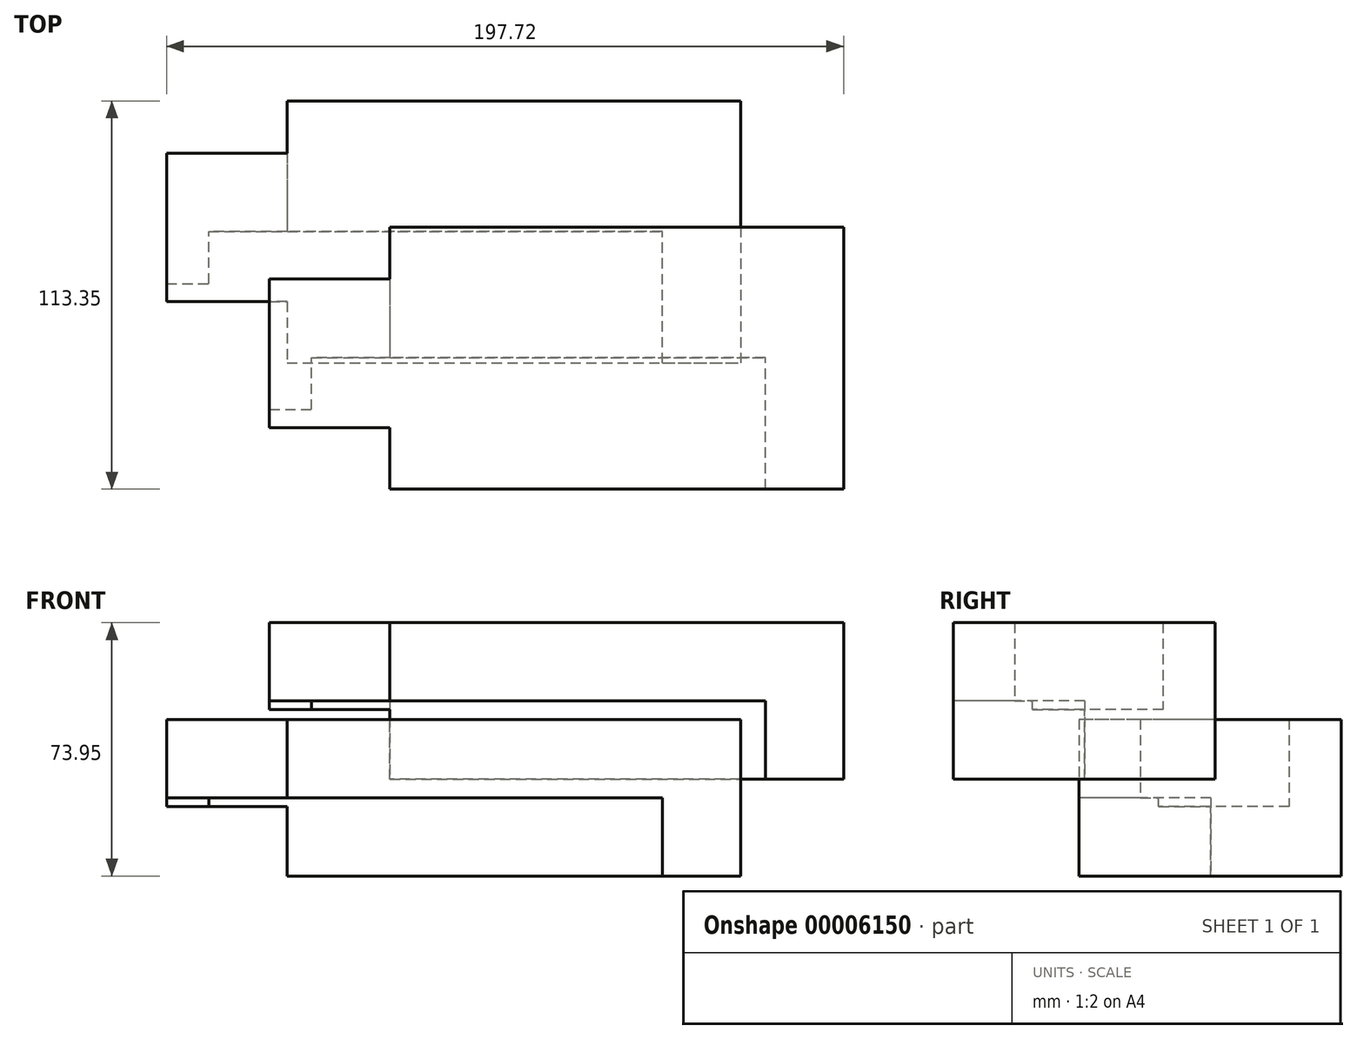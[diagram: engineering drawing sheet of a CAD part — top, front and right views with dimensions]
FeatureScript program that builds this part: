
annotation { "Feature Type Name" : "Feature", "Feature Type Description" : "" }
export const myFeature = defineFeature(function(context is Context, id is Id, definition is map)
    precondition{}
    {
        {
            var Q0;
            Q0=qCreatedBy(makeId("Top.planeOp"),FACE);
            var sketch = newSketch(context, id + "F0", { "sketchPlane" : qUnion([Q0])});
            skLineSegment(sketch, "E0.bottom", {"start": v(-122.75, 38.02) * mm, "end": v(9.77, 38.02) * mm});
            skLineSegment(sketch, "E0.top", {"start": v(-122.75, -38.52) * mm, "end": v(9.77, -38.52) * mm});
            skLineSegment(sketch, "E0.left", {"start": v(-122.75, 38.02) * mm, "end": v(-122.75, -38.52) * mm});
            skLineSegment(sketch, "E0.right", {"start": v(9.77, 38.02) * mm, "end": v(9.77, -38.52) * mm});
            skSolve(sketch);
        }
        {
            var Q0;
            Q0=makeQuery(id+"F0.imprint","IMPRINT",FACE,{"disambiguationData":[TD([[makeQuery(id+"F0.imprint","IMPRINT",EDGE,{"derivedFrom":sQuery(id+"F0.wireOp",EDGE,"E0.bottom")}),-1.0]])]});
            extrude(context, id + "F1", {"entities" : qUnion([Q0]), "depth" : 45.72 * mm});
        }
        {
            var Q0;
            Q0=makeQuery(id+"F1.opExtrude","CAP_FACE",FACE,{"disambiguationData":[OSD([sQuery(id+"F0.wireOp",EDGE,"E0.bottom"),sQuery(id+"F0.wireOp",EDGE,"E0.top"),sQuery(id+"F0.wireOp",EDGE,"E0.left"),sQuery(id+"F0.wireOp",EDGE,"E0.right")])],"isStart":false});
            var sketch = newSketch(context, id + "F2", { "sketchPlane" : qUnion([Q0])});
            skLineSegment(sketch, "E1.bottom", {"start": v(-157.9, 22.79) * mm, "end": v(-42.09, 22.79) * mm});
            skLineSegment(sketch, "E1.top", {"start": v(-157.9, -20.6) * mm, "end": v(-42.09, -20.6) * mm});
            skLineSegment(sketch, "E1.left", {"start": v(-157.9, 22.79) * mm, "end": v(-157.9, -20.6) * mm});
            skLineSegment(sketch, "E1.right", {"start": v(-42.09, 22.79) * mm, "end": v(-42.09, -20.6) * mm});
            skLineSegment(sketch, "E2.bottom", {"start": v(-36.24, -5.32) * mm, "end": v(-3.16, -5.32) * mm});
            skLineSegment(sketch, "E2.top", {"start": v(-36.24, 22.77) * mm, "end": v(-3.16, 22.77) * mm});
            skLineSegment(sketch, "E2.left", {"start": v(-36.24, -5.32) * mm, "end": v(-36.24, 22.77) * mm});
            skLineSegment(sketch, "E2.right", {"start": v(-3.16, -5.32) * mm, "end": v(-3.16, 22.77) * mm});
            skSolve(sketch);
        }
        {
            var Q0;
            Q0 = qSketchRegion(id + "F2", true);
            extrude(context, id + "F3", {"entities" : qUnion([Q0]), "operationType" : NewBodyOperationType.ADD, "oppositeDirection" : true, "depth" : 25.4 * mm});
        }
        {
            var Q0;
            Q0=makeQuery(id+"F1.opExtrude","SWEPT_BODY",BODY,{"disambiguationData":[OSD([sQuery(id+"F0.wireOp",EDGE,"E0.bottom"),sQuery(id+"F0.wireOp",EDGE,"E0.top"),sQuery(id+"F0.wireOp",EDGE,"E0.left"),sQuery(id+"F0.wireOp",EDGE,"E0.right")])]});
            transform(context, id + "F4", {"entities" : qUnion([Q0]), "transformType" : TransformType.TRANSLATION_3D, "dx" : 22.86 * mm, "dy" : 38.1 * mm, "dz" : 22.86 * mm, "makeCopy" : true});
        }
        {
            var Q0;
            Q0=makeQuery(id+"F1.opExtrude","SWEPT_BODY",BODY,{"disambiguationData":[OSD([sQuery(id+"F0.wireOp",EDGE,"E0.bottom"),sQuery(id+"F0.wireOp",EDGE,"E0.top"),sQuery(id+"F0.wireOp",EDGE,"E0.left"),sQuery(id+"F0.wireOp",EDGE,"E0.right")])]});
            var Q1;
            Q1=makeQuery(id+"F4.opPattern","COPY",BODY,{"derivedFrom":makeQuery(id+"F1.opExtrude","SWEPT_BODY",BODY,{"disambiguationData":[OSD([sQuery(id+"F0.wireOp",EDGE,"E0.bottom"),sQuery(id+"F0.wireOp",EDGE,"E0.top"),sQuery(id+"F0.wireOp",EDGE,"E0.left"),sQuery(id+"F0.wireOp",EDGE,"E0.right")])]}),"instanceName":"1"});
            booleanBodies(context, id + "F5", {"operationType" : BooleanOperationType.SUBTRACTION, "tools" : qUnion([Q0]), "targets" : qUnion([Q1])});
        }
        {
            var Q0;
            Q0=makeQuery(id+"F4.opPattern","COPY",BODY,{"derivedFrom":makeQuery(id+"F1.opExtrude","SWEPT_BODY",BODY,{"disambiguationData":[OSD([sQuery(id+"F0.wireOp",EDGE,"E0.bottom"),sQuery(id+"F0.wireOp",EDGE,"E0.top"),sQuery(id+"F0.wireOp",EDGE,"E0.left"),sQuery(id+"F0.wireOp",EDGE,"E0.right")])]}),"instanceName":"1"});
            transform(context, id + "F6", {"entities" : qUnion([Q0]), "transformType" : TransformType.TRANSLATION_3D, "dx" : 30.05 * mm, "dy" : -36.8 * mm, "dz" : 28.23 * mm, "makeCopy" : true});
        }
    });
